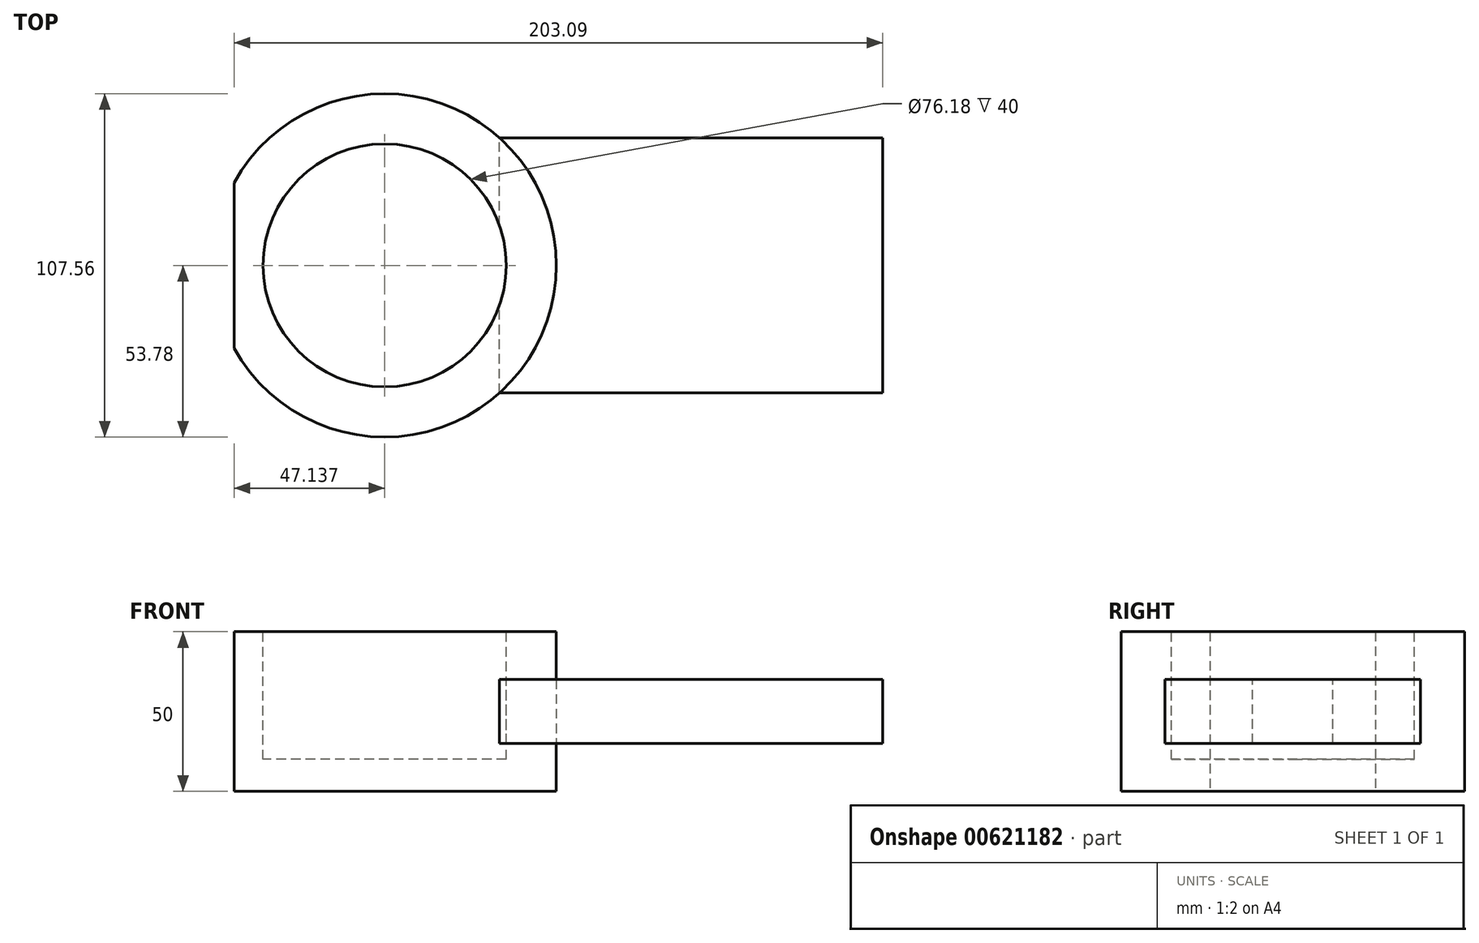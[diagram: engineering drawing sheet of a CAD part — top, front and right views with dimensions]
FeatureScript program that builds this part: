
annotation { "Feature Type Name" : "Feature", "Feature Type Description" : "" }
export const myFeature = defineFeature(function(context is Context, id is Id, definition is map)
    precondition{}
    {
        {
            var Q0;
            Q0=qCreatedBy(makeId("Top.planeOp"),FACE);
            var sketch = newSketch(context, id + "F0", { "sketchPlane" : qUnion([Q0])});
            skLineSegment(sketch, "E0.bottom", {"start": v(0, 0) * mm, "end": v(120, 0) * mm});
            skLineSegment(sketch, "E0.top", {"start": v(0, 80) * mm, "end": v(120, 80) * mm});
            skLineSegment(sketch, "E0.left", {"start": v(0, 0) * mm, "end": v(0, 80) * mm});
            skLineSegment(sketch, "E0.right", {"start": v(120, 0) * mm, "end": v(120, 80) * mm});
            skPoint(sketch, "E1.middle", {"position": v(50, 40) * mm});
            skCircle(sketch, "E2", {"center": v(-35.95, 40) * mm, "radius": 53.78 * mm});
            skPoint(sketch, "E2.third.point", {"position": v(-89.74, 40) * mm});
            skPoint(sketch, "E2.third.point.positionSnap0", {"position": v(0, 40) * mm});
            skLineSegment(sketch, "E3", {"start": v(-83.09, 65.9) * mm, "end": v(-83.09, 14.1) * mm});
            skSolve(sketch);
        }
        {
            var Q0;
            {var subQ0=sQuery(id+"F0.wireOp",EDGE,"E0.left");Q0=makeQuery(id+"F0.imprint","IMPRINT",FACE,{"disambiguationData":[TD([[makeQuery(id+"F0.imprint","IMPRINT",EDGE,{"derivedFrom":subQ0}),1.0]])]});}
            var Q1;
            {var subQ0=sQuery(id+"F0.wireOp",EDGE,"E0.left");Q1=makeQuery(id+"F0.imprint","IMPRINT",FACE,{"disambiguationData":[TD([[makeQuery(id+"F0.imprint","IMPRINT",EDGE,{"derivedFrom":subQ0}),-1.0]])]});}
            extrude(context, id + "F1", {"entities" : qUnion([Q0, Q1]), "depth" : 25 * mm, "offsetDistance" : 25 * mm, "hasSecondDirection" : true, "secondDirectionOppositeDirection" : true, "secondDirectionDepth" : 25 * mm});
        }
        {
            var Q0;
            {var subQ0=sQuery(id+"F0.wireOp",EDGE,"E0.bottom");Q0=makeQuery(id+"F0.imprint","IMPRINT",FACE,{"disambiguationData":[TD([[makeQuery(id+"F0.imprint","IMPRINT",EDGE,{"derivedFrom":subQ0}),1.0]])]});}
            var Q1;
            {var subQ0=sQuery(id+"F0.wireOp",EDGE,"E0.left");Q1=makeQuery(id+"F0.imprint","IMPRINT",FACE,{"disambiguationData":[TD([[makeQuery(id+"F0.imprint","IMPRINT",EDGE,{"derivedFrom":subQ0}),-1.0]])]});}
            extrude(context, id + "F2", {"entities" : qUnion([Q0, Q1]), "depth" : 10 * mm, "offsetDistance" : 25 * mm, "hasSecondDirection" : true, "secondDirectionOppositeDirection" : true, "secondDirectionDepth" : 10 * mm});
        }
        {
            var Q0;
            Q0=makeQuery(id+"F1.opExtrude","CAP_FACE",FACE,{"disambiguationData":[OSD([sQuery(id+"F0.wireOp",EDGE,"E2"),sQuery(id+"F0.wireOp",EDGE,"E3")])],"isStart":false});
            var sketch = newSketch(context, id + "F3", { "sketchPlane" : qUnion([Q0])});
            skLineSegment(sketch, "E4", {"start": v(-35.95, 93.78) * mm, "end": v(-35.95, -13.78) * mm});
            skLineSegment(sketch, "E5", {"start": v(-83.09, 40) * mm, "end": v(17.83, 40) * mm});
            skPoint(sketch, "E6", {"position": v(-35.95, 40) * mm});
            skCircle(sketch, "E7", {"center": v(-35.95, 40) * mm, "radius": 38.09 * mm});
            skSolve(sketch);
        }
        {
            var Q0;
            Q0 = qSketchRegion(id + "F3", true);
            extrude(context, id + "F4", {"entities" : qUnion([Q0]), "operationType" : NewBodyOperationType.REMOVE, "oppositeDirection" : true, "depth" : 40 * mm, "offsetDistance" : 25 * mm});
        }
    });
